FCSTD DOCUMENT  (FreeCAD 0.17R11939 (Git))
Label: milling_saw_sketch
License: All rights reserved
LicenseURL: http://en.wikipedia.org/wiki/All_rights_reserved
objects: Sketcher::SketchObject×1, PartDesign::Body×1
note: 2 computed .brp shape members not serialized (recipe doc carries the construction recipe); baked Part::Feature solids carry a one-line shape summary decoded from their .brp

FEATURE [Sketcher::SketchObject] Sketch
  MapMode = 5
  Support = -> [XY_Plane]
  sketch-geometry (8):
    g0: Circle CenterX=0 CenterY=0 CenterZ=0 NormalX=0 NormalY=0 NormalZ=1 Radius=28.575
    g1: Circle CenterX=0 CenterY=0 CenterZ=0 NormalX=0 NormalY=0 NormalZ=1 Radius=9.525
    g2: LineSegment StartX=11.4052 StartY=-7.22028 StartZ=0 EndX=30.4552 EndY=-7.22028 EndZ=0
    g3: LineSegment StartX=30.4552 StartY=-7.22028 StartZ=0 EndX=30.4552 EndY=-107.22 EndZ=0
    g4: LineSegment StartX=30.4552 StartY=-107.22 StartZ=0 EndX=11.4052 EndY=-107.22 EndZ=0
    g5: LineSegment StartX=11.4052 StartY=-107.22 StartZ=0 EndX=11.4052 EndY=-7.22028 EndZ=0
    g6: Circle CenterX=8.90521 CenterY=-13.6783 CenterZ=0 NormalX=0 NormalY=0 NormalZ=1 Radius=5
    g7: LineSegment StartX=12.6498 StartY=-7.22028 StartZ=0 EndX=12.6498 EndY=-107.22 EndZ=0
  constraints (21):
    c: Coincident(g0,g-1)
    c: Radius(g0) = 28.575
    c: Coincident(g1,g-1)
    c: Radius(g1) = 9.525
    c: Coincident(g2,g3)
    c: Coincident(g3,g4)
    c: Coincident(g4,g5)
    c: Coincident(g5,g2)
    c: Horizontal(g2)
    c: Horizontal(g4)
    c: Vertical(g3)
    c: Vertical(g5)
    c: Distance(g4) = 19.05
    c: Distance(g3) = 100
    c: DistanceX(g6,g2) = 2.5
    c: DistanceY(g6,g2) = 6.45799
    c: Radius(g6) = 5
    c: PointOnObject(g7,g2)
    c: PointOnObject(g7,g4)
    c: Vertical(g7)
    c: Distance(g7,g4) = 1.2446
FEATURE [PartDesign::Body] Body
  Group = -> [Sketch]
  Origin = -> Origin
